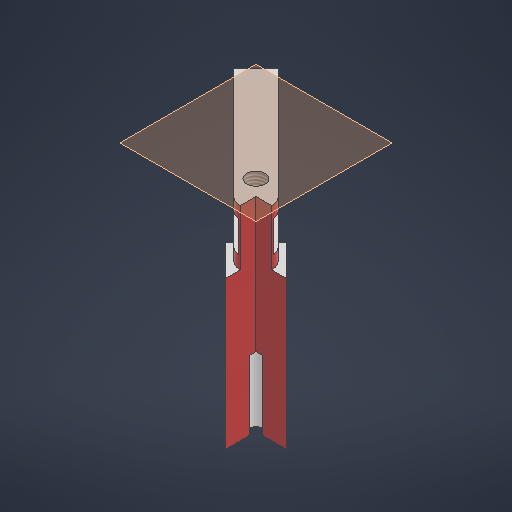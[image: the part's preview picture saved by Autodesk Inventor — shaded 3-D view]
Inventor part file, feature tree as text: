
AUTODESK INVENTOR PART (.ipt)
format: ipt  version: 2025.1 (Build 291241000, 241)  size: 677,376 bytes
history: native  units: in
note: dims shown in document units (in); Inventor stores cm internally (conversion verified against a paired STEP export)
features: projected_geometry x32, sketch x14, extrude x10, plane x1, thread x1, other x1
ambient origin geometry x8: Origin, YZ Plane, XZ Plane, XY Plane, X Axis, Y Axis, Z Axis, Center Point
bodies: Solid1 (feature_tree)
feature tree (59):
  extrude  "Extrusion1"  Depth=0.2in TaperAngle=0.0deg
  extrude  "Extrusion2"  TaperAngle=135.0deg  [1 undecoded]
  sketch  "Sketch3"  dims[d5=0.2362in d6=0.0in d7=0.1575in]
  extrude  "Extrusion5"  Depth=0.1575in
  sketch  "Sketch6"  dims[d8=0.1969in d11=0.2362in]
  plane  "Work Plane3"
  extrude  "Extrusion7"  Depth=0.2362in
  extrude  "Extrusion9"  Depth=0.0394in
  extrude  "Extrusion10"  Depth=0.2362in TaperAngle=0.0deg
  extrude  "Extrusion12"  Depth=0.0591in TaperAngle=0.0deg
  extrude  "Extrusion13"  Depth=0.3937in TaperAngle=0.0deg
  extrude  "Extrusion14"  Depth=0.1969in
  thread  "Thread2"  [1 undecoded]
  extrude  "Extrusion15"  Depth=0.315in TaperAngle=0.0deg
  sketch  "Sketch17"  dims[d52=45.0deg]
  sketch  "Sketch18"  dims[d53=0.315in d54=0.0in]
  sketch  "Sketch19"  dims[d55=0.8608in]
  sketch  "Sketch1"  dims[d0=0.2in d1=1.0in d2=0.0in]
  sketch  "Sketch2"  dims[d3=1.0in d4=135.0deg]
  sketch  "Sketch7"  dims[d14=1.3312in d15=0.0in d16=0.0394in]
  sketch  "Sketch10"  dims[d19=0.1181in d20=0.2362in d21=0.0in]
  sketch  "Sketch11"  dims[d29=0.0591in d30=0.0in d31=0.0591in d32=0.0in]
  projected_geometry  "Projected Loop1"
  sketch  "Sketch13"  dims[d37=0.3937in d38=1.2534in d39=0.0in]
  sketch  "Sketch14"  dims[d40=0.1969in d41=0.1969in d42=0.0787in]
  sketch  "Sketch15"  dims[d43=0.4409in d44=0.0in d48=0.315in d49=0.0in]
  sketch  "Sketch16"  dims[d50=0.315in d51=0.0in]
  projected_geometry  "Projected Loop2"
  projected_geometry  "Projected Loop3"
  projected_geometry  "Projected Loop4"
  projected_geometry  "Projected Loop5"
  projected_geometry  "Projected Loop6"
  projected_geometry  "Projected Loop7"
  projected_geometry  "Projected Loop8"
  projected_geometry  "Projected Loop9"
  projected_geometry  "Projected Loop10"
  projected_geometry  "Projected Loop11"
  projected_geometry  "Projected Loop12"
  projected_geometry  "Projected Loop13"
  projected_geometry  "Projected Loop14"
  projected_geometry  "Projected Loop15"
  projected_geometry  "Projected Loop16"
  projected_geometry  "Projected Loop17"
  projected_geometry  "Projected Loop18"
  projected_geometry  "Projected Loop19"
  projected_geometry  "Projected Loop20"
  projected_geometry  "Projected Loop21"
  projected_geometry  "Projected Loop22"
  projected_geometry  "Projected Loop23"
  projected_geometry  "Projected Loop24"
  projected_geometry  "Projected Loop25"
  projected_geometry  "Projected Loop26"
  projected_geometry  "Projected Loop27"
  projected_geometry  "Projected Loop28"
  projected_geometry  "Projected Loop29"
  projected_geometry  "Projected Loop30"
  projected_geometry  "Projected Loop31"
  projected_geometry  "Projected Loop32"
  other  "Finish1"
note: 2 required parameter values undecoded (feature->parameter linkage not recoverable at this tier; creation-order binding heuristic only, values carry confidence <= 0.55)
